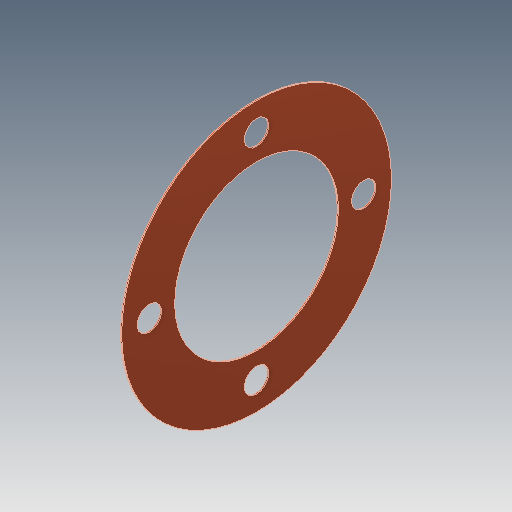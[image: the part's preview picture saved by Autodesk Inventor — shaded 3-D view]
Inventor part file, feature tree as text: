
AUTODESK INVENTOR PART (.ipt)
format: ipt  version: 2025 (Build 290162000, 162)  size: 103,424 bytes
history: native  units: in
note: dims shown in document units (in); Inventor stores cm internally (conversion verified against a paired STEP export)
features: sketch x2, extrude x1
ambient origin geometry x8: Origin, YZ Plane, XZ Plane, XY Plane, X Axis, Y Axis, Z Axis, Center Point
bodies: 实体1 (feature_tree)
feature tree (3):
  extrude  "拉伸1"  Depth=2.9134in
  sketch  "草图1"  dims[d0=0.4331in d2=2.9134in]
  sketch  "草图 - 环形阵列1"  dims[d1=4.8031in d3=2.9134in d4=0.4331in d5=1.9094in d6=1.5748in d8=360.0deg d10=0.0197in d11=0.0in]
